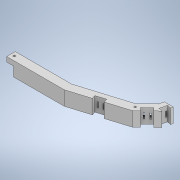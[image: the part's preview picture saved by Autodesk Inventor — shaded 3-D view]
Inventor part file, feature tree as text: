
AUTODESK INVENTOR PART (.ipt)
format: ipt  version: 2020 (Build 240168000, 168)  size: 319,488 bytes
history: native  units: mm
features: sketch x10, extrude x8, projected_geometry x8, hole x2
ambient origin geometry x8: Origin, YZ Plane, XZ Plane, XY Plane, X Axis, Y Axis, Z Axis, Center Point
bodies: Body1 (feature_tree)
feature tree (28):
  extrude  "돌출11"  Depth=657.5mm
  extrude  "돌출12"  Depth=667.5mm
  extrude  "돌출13"  Depth=585.0mm
  extrude  "돌출14"  Depth=0.872665mm
  extrude  "돌출15"  Depth=1299.898854mm
  extrude  "돌출16"  Depth=2.356194mm
  extrude  "돌출17"  Depth=2.356194mm
  extrude  "돌출18"  Depth=999.812583mm
  hole  "구멍3"  [1 undecoded]
  hole  "구멍4"  [1 undecoded]
  sketch  "스케치1"
  sketch  "스케치14"
  projected_geometry  "투영된 루프10"
  sketch  "스케치15"
  projected_geometry  "투영된 루프11"
  sketch  "스케치16"
  projected_geometry  "투영된 루프12"
  sketch  "스케치17"
  projected_geometry  "투영된 루프13"
  sketch  "스케치18"
  projected_geometry  "투영된 루프14"
  sketch  "스케치19"
  projected_geometry  "투영된 루프15"
  sketch  "스케치20"
  projected_geometry  "투영된 루프16"
  sketch  "스케치21"
  sketch  "스케치22"
  projected_geometry  "투영된 루프17"
note: 2 required parameter values undecoded (feature->parameter linkage not recoverable at this tier; creation-order binding heuristic only, values carry confidence <= 0.55)
